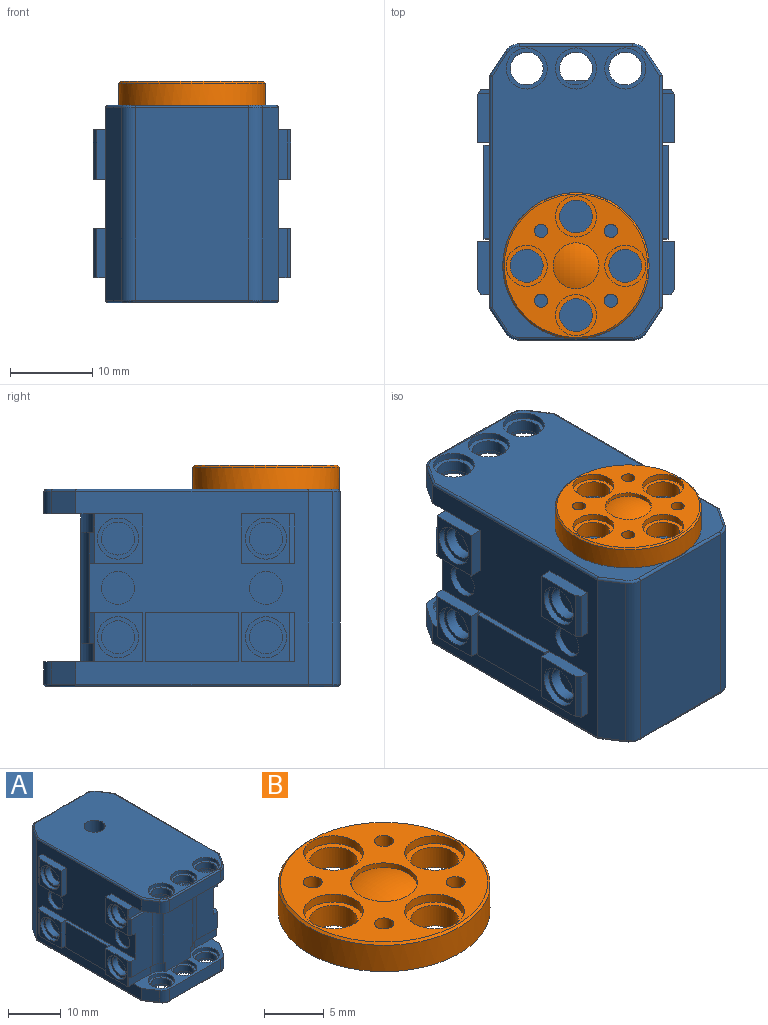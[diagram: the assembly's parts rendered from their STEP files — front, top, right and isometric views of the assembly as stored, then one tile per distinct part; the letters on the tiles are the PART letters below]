
ASSEMBLY  parts=2 mates=1
PART A: 203 faces, bbox 24x36x24 mm
  f0: cylinder r=8.9mm len=3.75mm, axis (0,0,1), area 0mm2, adj f1,f138
  f1: plane 35.6x20.4mm, normal (0,0,1), area 633.5mm2, adj f0,f38,f39,f40,f42,f43,f44,f61
  f2: plane 4x4mm, normal (1,0,0), area 12.6mm2, adj f10
  f3: plane 4x4mm, normal (1,0,0), area 12.6mm2, adj f11
  f4: plane 4x4mm, normal (1,0,0), area 12.6mm2, adj f12
  f5: plane 4x4mm, normal (1,0,0), area 12.6mm2, adj f13
  f6: plane 4x4mm, normal (-1,0,0), area 12.6mm2, adj f14
  f7: plane 4x4mm, normal (-1,0,0), area 12.6mm2, adj f15
  f8: plane 4x4mm, normal (-1,0,0), area 12.6mm2, adj f16
  f9: plane 4x4mm, normal (-1,0,0), area 12.6mm2, adj f17
  f10: cylinder r=2mm len=4mm, axis (1,0,0), area 17.6mm2, adj f2,f18
  f11: cylinder r=2mm len=4mm, axis (1,0,0), area 17.6mm2, adj f3,f19
  f12: cylinder r=2mm len=4mm, axis (1,0,0), area 17.6mm2, adj f4,f20
  f13: cylinder r=2mm len=4mm, axis (1,0,0), area 17.6mm2, adj f5,f21
  f14: cylinder r=2mm len=4mm, axis (1,0,0), area 17.6mm2, adj f6,f28
  f15: cylinder r=2mm len=4mm, axis (1,0,0), area 17.6mm2, adj f7,f29
  f16: cylinder r=2mm len=4mm, axis (1,0,0), area 17.6mm2, adj f8,f31
  f17: cylinder r=2mm len=4mm, axis (1,0,0), area 17.6mm2, adj f9,f32
  f18: plane 5x5mm, normal (1,0,0), area 7.1mm2, adj f10,f34
  f19: plane 5x5mm, normal (1,0,0), area 7.1mm2, adj f11,f35
  f20: plane 5x5mm, normal (1,0,0), area 7.1mm2, adj f12,f36
  f21: plane 5x5mm, normal (1,0,0), area 7.1mm2, adj f13,f37
  f22: plane 5x5mm, normal (0,0,1), area 7.1mm2, adj f26,f38
  f23: plane 5x5mm, normal (0,0,1), area 7.1mm2, adj f25,f39
  f24: plane 5x5mm, normal (0,0,1), area 7.1mm2, adj f27,f40
  f25: cylinder r=2mm len=4mm, axis (0,0,1), area 17.6mm2, adj f23,f41
  f26: cylinder r=2mm len=4mm, axis (0,0,1), area 17.6mm2, adj f22,f45
  f27: cylinder r=2mm len=4mm, axis (0,0,1), area 17.6mm2, adj f24,f46
  f28: plane 5x5mm, normal (-1,0,0), area 7.1mm2, adj f14,f47
  f29: plane 5x5mm, normal (-1,0,0), area 7.1mm2, adj f15,f48
  f30: plane 4x1mm, normal (0,0,1), area 2.8mm2, adj f49,f74
  f31: plane 5x5mm, normal (-1,0,0), area 7.1mm2, adj f16,f50
  f32: plane 5x5mm, normal (-1,0,0), area 7.1mm2, adj f17,f51
  f33: plane 4x1mm, normal (0,0,-1), area 2.8mm2, adj f49,f91
  f34: cylinder r=2.5mm len=5mm, axis (1,0,0), area 12.6mm2, adj f18,f54
  f35: cylinder r=2.5mm len=5mm, axis (1,0,0), area 12.6mm2, adj f19,f60
  f36: cylinder r=2.5mm len=5mm, axis (1,0,0), area 12.6mm2, adj f20,f63
  f37: cylinder r=2.5mm len=5mm, axis (1,0,0), area 12.6mm2, adj f21,f65
  f38: cylinder r=2.5mm len=5mm, axis (0,0,1), area 12.6mm2, adj f1,f22
  f39: cylinder r=2.5mm len=5mm, axis (0,0,1), area 12.6mm2, adj f1,f23
  f40: cylinder r=2.5mm len=5mm, axis (0,0,1), area 12.6mm2, adj f1,f24
  f41: plane 5x5mm, normal (0,0,-1), area 7.1mm2, adj f25,f74
  f42: revolved ~1.68x1.07mm, area 0.9mm2, adj f1,f43,f73,f77
  f43: cylinder r=0.3mm len=13.83mm, axis (1,0,0), area 6.5mm2, adj f1,f42,f44,f78
  f44: revolved ~1.68x1.07mm, area 0.9mm2, adj f1,f43,f61,f79
  f45: plane 5x5mm, normal (0,0,-1), area 7.1mm2, adj f26,f82
  f46: plane 5x5mm, normal (0,0,-1), area 7.1mm2, adj f27,f83
  f47: cylinder r=2.5mm len=5mm, axis (1,0,0), area 12.6mm2, adj f28,f84
  f48: cylinder r=2.5mm len=5mm, axis (1,0,0), area 12.6mm2, adj f29,f90
  f49: plane 18x8mm, normal (0,-1,0), area 138.4mm2, adj f30,f33,f56,f57,f58,f75,f81,f86
  f50: cylinder r=2.5mm len=5mm, axis (1,0,0), area 12.6mm2, adj f31,f99
  f51: cylinder r=2.5mm len=5mm, axis (1,0,0), area 12.6mm2, adj f32,f101
  f52: revolved ~1.68x1.07mm, area 0.9mm2, adj f111,f186,f187,f200
  f53: revolved ~1.68x1.07mm, area 0.9mm2, adj f112,f187,f188,f200
  f54: plane 6x5.84mm, normal (1,0,0), area 15.4mm2, adj f34,f59,f114,f115,f116
  f55: plane 6x0.66mm, normal (0.84,-0.54,0), area 3.3mm2, adj f56,f60,f80,f117,f118,f120
  f56: plane 8.54x1.53mm, normal (0,0,1), area 4.5mm2, adj f49,f55,f57,f80,f81,f117
  f57: cylinder r=2.5mm len=13.5mm, axis (0,0,1), area 31.3mm2, adj f49,f56,f58,f117
  f58: plane 8.54x1.53mm, normal (0,0,-1), area 4.5mm2, adj f49,f57,f59,f94,f95,f117
  f59: plane 6x0.66mm, normal (0.84,-0.54,0), area 3.3mm2, adj f54,f58,f94,f114,f116,f117
  f60: plane 6x5.84mm, normal (1,0,0), area 15.4mm2, adj f35,f55,f118,f119,f120
  f61: cylinder r=0.3mm len=3.1mm, axis (0.54,0.84,0), area 1.6mm2, adj f1,f44,f113,f121
  f62: plane 6x0.66mm, normal (0.84,0.54,0), area 4.7mm2, adj f63,f122,f123,f124
  f63: plane 6x5.84mm, normal (1,0,0), area 15.4mm2, adj f36,f62,f122,f124,f125
  f64: plane 6x0.66mm, normal (0.84,0.54,0), area 4.7mm2, adj f65,f126,f127,f128
  f65: plane 6x5.84mm, normal (1,0,0), area 15.4mm2, adj f37,f64,f126,f128,f129
  f66: plane 4x4mm, normal (1,0,0), area 12.6mm2, adj f130
  f67: plane 4x4mm, normal (1,0,0), area 12.6mm2, adj f131
  f68: plane 11.4x6mm, normal (1,0,0), area 68.4mm2, adj f132,f133,f134,f135
  f69: revolved ~1.68x1.07mm, area 0.9mm2, adj f137,f190,f191,f200
  f70: revolved ~1.68x1.07mm, area 0.9mm2, adj f1,f136,f137,f138
  f71: revolved ~1.68x1.07mm, area 0.9mm2, adj f139,f191,f192,f200
  f72: revolved ~1.68x1.07mm, area 0.9mm2, adj f1,f138,f139,f140
  f73: cylinder r=0.3mm len=3.1mm, axis (0.54,-0.84,0), area 1.6mm2, adj f1,f42,f141,f142
  f74: cylinder r=2.5mm len=5mm, axis (0,0,1), area 12.6mm2, adj f30,f41,f143
  f75: cylinder r=3.02mm len=2.63mm, axis (0,0,1), area 7.2mm2, adj f49,f76,f88,f143
  f76: plane 5.91x2.25mm, normal (0,-1,0), area 13.3mm2, adj f75,f88,f89,f143,f144
  f77: cylinder r=2mm len=2.7mm, axis (0,0,1), area 5.4mm2, adj f42,f78,f142,f143
  f78: plane 13.83x2.7mm, normal (0,-1,0), area 37.3mm2, adj f43,f77,f79,f143
  f79: cylinder r=2mm len=2.7mm, axis (0,0,1), area 5.4mm2, adj f44,f78,f121,f143
  f80: plane 5.91x2.25mm, normal (0,-1,0), area 13.3mm2, adj f55,f56,f81,f120,f143
  f81: cylinder r=3.02mm len=2.63mm, axis (0,0,1), area 7.2mm2, adj f49,f56,f80,f143
  f82: cylinder r=2.5mm len=5mm, axis (0,0,1), area 12.6mm2, adj f45,f143
  f83: cylinder r=2.5mm len=5mm, axis (0,0,1), area 12.6mm2, adj f46,f143
  f84: plane 6x5.84mm, normal (-1,0,0), area 15.4mm2, adj f47,f89,f144,f145,f146
  f85: plane 6x0.66mm, normal (-0.84,-0.54,0), area 3.3mm2, adj f86,f90,f93,f147,f148,f150
  f86: plane 8.54x1.53mm, normal (0,0,-1), area 4.5mm2, adj f49,f85,f87,f92,f93,f147
  f87: cylinder r=2.5mm len=13.5mm, axis (0,0,1), area 31.3mm2, adj f49,f86,f88,f147
  f88: plane 8.54x1.53mm, normal (0,0,1), area 4.5mm2, adj f49,f75,f76,f87,f89,f147
  f89: plane 6x0.66mm, normal (-0.84,-0.54,0), area 3.3mm2, adj f76,f84,f88,f144,f146,f147
  f90: plane 6x5.84mm, normal (-1,0,0), area 15.4mm2, adj f48,f85,f148,f149,f150
  f91: cylinder r=2.5mm len=5mm, axis (0,0,1), area 12.6mm2, adj f33,f109,f151
  f92: cylinder r=3.02mm len=2.63mm, axis (0,0,1), area 7.2mm2, adj f49,f86,f93,f151
  f93: plane 5.91x2.25mm, normal (0,-1,0), area 13.3mm2, adj f85,f86,f92,f150,f151
  f94: plane 5.91x2.25mm, normal (0,-1,0), area 13.3mm2, adj f58,f59,f95,f114,f151
  f95: cylinder r=3.02mm len=2.63mm, axis (0,0,1), area 7.2mm2, adj f49,f58,f94,f151
  f96: cylinder r=2.5mm len=5mm, axis (0,0,1), area 12.6mm2, adj f108,f151
  f97: cylinder r=2.5mm len=5mm, axis (0,0,1), area 12.6mm2, adj f110,f151
  f98: plane 6x0.66mm, normal (-0.84,0.54,0), area 4.7mm2, adj f99,f152,f153,f154
  f99: plane 6x5.84mm, normal (-1,0,0), area 15.4mm2, adj f50,f98,f152,f154,f155
  f100: plane 6x0.66mm, normal (-0.84,0.54,0), area 4.7mm2, adj f101,f156,f157,f158
  f101: plane 6x5.84mm, normal (-1,0,0), area 15.4mm2, adj f51,f100,f156,f158,f159
  f102: plane 4x4mm, normal (-1,0,0), area 12.6mm2, adj f160
  f103: plane 4x4mm, normal (-1,0,0), area 12.6mm2, adj f161
  f104: plane 11.4x6mm, normal (-1,0,0), area 68.4mm2, adj f162,f163,f164,f165
  f105: plane 4x4mm, normal (0,0,-1), area 12.6mm2, adj f166
  f106: plane 4x4mm, normal (0,0,-1), area 12.6mm2, adj f167
  f107: plane 4x4mm, normal (0,0,-1), area 12.6mm2, adj f168
  f108: plane 5x5mm, normal (0,0,1), area 7.1mm2, adj f96,f169
  f109: plane 5x5mm, normal (0,0,1), area 7.1mm2, adj f91,f170
  f110: plane 5x5mm, normal (0,0,1), area 7.1mm2, adj f97,f171
  f111: cylinder r=2mm len=2.7mm, axis (0,0,1), area 5.4mm2, adj f52,f151,f172,f173
  f112: cylinder r=2mm len=2.7mm, axis (0,0,1), area 5.4mm2, adj f53,f151,f173,f174
  f113: cylinder r=0.3mm len=28.3mm, axis (0,1,0), area 13.3mm2, adj f1,f61,f136,f175
  f114: plane 5.98x1.5mm, normal (0,0,-1), area 9mm2, adj f54,f59,f94,f115,f175
  f115: plane 6x1.5mm, normal (0,1,0), area 9mm2, adj f54,f114,f116,f175
  f116: plane 6.5x1.5mm, normal (0,0,1), area 9.6mm2, adj f54,f59,f115,f117,f175
  f117: plane 13.5x5.57mm, normal (0,-1,0), area 68.8mm2, adj f55,f56,f57,f58,f59,f116,f118,f175
  f118: plane 6.5x1.5mm, normal (0,0,-1), area 9.6mm2, adj f55,f60,f117,f119,f175
  f119: plane 6x1.5mm, normal (0,1,0), area 9mm2, adj f60,f118,f120,f175
  f120: plane 5.98x1.5mm, normal (0,0,1), area 9mm2, adj f55,f60,f80,f119,f175
  f121: plane 2.94x2.7mm, normal (0.84,-0.54,0), area 9.5mm2, adj f61,f79,f143,f175
  f122: plane 6.5x1.5mm, normal (0,0,-1), area 9.6mm2, adj f62,f63,f123,f125,f175
  f123: plane 6x1.07mm, normal (0,1,0), area 6.4mm2, adj f62,f122,f124,f175
  f124: plane 6.5x1.5mm, normal (0,0,1), area 9.6mm2, adj f62,f63,f123,f125,f175
  f125: plane 6x1.5mm, normal (0,-1,0), area 9mm2, adj f63,f122,f124,f175
  f126: plane 6.5x1.5mm, normal (0,0,-1), area 9.6mm2, adj f64,f65,f127,f129,f175
  f127: plane 6x1.07mm, normal (0,1,0), area 6.4mm2, adj f64,f126,f128,f175
  f128: plane 6.5x1.5mm, normal (0,0,1), area 9.6mm2, adj f64,f65,f127,f129,f175
  f129: plane 6x1.5mm, normal (0,-1,0), area 9mm2, adj f65,f126,f128,f175
  f130: cylinder r=2mm len=4mm, axis (1,0,0), area 10.1mm2, adj f66,f175
  f131: cylinder r=2mm len=4mm, axis (1,0,0), area 10.1mm2, adj f67,f175
  f132: plane 11.4x0.7mm, normal (0,0,1), area 8mm2, adj f68,f133,f135,f175
  f133: plane 6x0.7mm, normal (0,-1,0), area 4.2mm2, adj f68,f132,f134,f175
  f134: plane 11.4x0.7mm, normal (0,0,-1), area 8mm2, adj f68,f133,f135,f175
  f135: plane 6x0.7mm, normal (0,1,0), area 4.2mm2, adj f68,f132,f134,f175
  f136: cylinder r=0.3mm len=3.1mm, axis (-0.54,0.84,0), area 1.6mm2, adj f1,f70,f113,f176
  f137: cylinder r=2mm len=23.4mm, axis (0,0,-1), area 46.6mm2, adj f69,f70,f176,f177
  f138: cylinder r=0.3mm len=13.83mm, axis (-1,0,0), area 6mm2, adj f0,f1,f70,f72,f177
  f139: cylinder r=2mm len=23.4mm, axis (0,0,-1), area 46.6mm2, adj f71,f72,f177,f178
  f140: cylinder r=0.3mm len=3.1mm, axis (-0.54,-0.84,0), area 1.6mm2, adj f1,f72,f141,f178
  f141: cylinder r=0.3mm len=28.3mm, axis (0,-1,0), area 13.3mm2, adj f1,f73,f140,f179
  f142: plane 2.94x2.7mm, normal (-0.84,-0.54,0), area 9.5mm2, adj f73,f77,f143,f179
  f143: plane 21x6.03mm, normal (0,0,-1), area 47.8mm2, adj f49,f74,f75,f76,f77,f78,f79,f80
  f144: plane 5.98x1.5mm, normal (0,0,1), area 9mm2, adj f76,f84,f89,f145,f179
  f145: plane 6x1.5mm, normal (0,1,0), area 9mm2, adj f84,f144,f146,f179
  f146: plane 6.5x1.5mm, normal (0,0,-1), area 9.6mm2, adj f84,f89,f145,f147,f179
  f147: plane 13.5x5.57mm, normal (0,-1,0), area 68.8mm2, adj f85,f86,f87,f88,f89,f146,f148,f179
  f148: plane 6.5x1.5mm, normal (0,0,1), area 9.6mm2, adj f85,f90,f147,f149,f179
  f149: plane 6x1.5mm, normal (0,1,0), area 9mm2, adj f90,f148,f150,f179
  f150: plane 5.98x1.5mm, normal (0,0,-1), area 9mm2, adj f85,f90,f93,f149,f179
  f151: plane 21x6.03mm, normal (0,0,1), area 47.8mm2, adj f49,f91,f92,f93,f94,f95,f96,f97
  f152: plane 6.5x1.5mm, normal (0,0,1), area 9.6mm2, adj f98,f99,f153,f155,f179
  f153: plane 6x1.07mm, normal (0,1,0), area 6.4mm2, adj f98,f152,f154,f179
  f154: plane 6.5x1.5mm, normal (0,0,-1), area 9.6mm2, adj f98,f99,f153,f155,f179
  f155: plane 6x1.5mm, normal (0,-1,0), area 9mm2, adj f99,f152,f154,f179
  f156: plane 6.5x1.5mm, normal (0,0,1), area 9.6mm2, adj f100,f101,f157,f159,f179
  f157: plane 6x1.07mm, normal (0,1,0), area 6.4mm2, adj f100,f156,f158,f179
  f158: plane 6.5x1.5mm, normal (0,0,-1), area 9.6mm2, adj f100,f101,f157,f159,f179
  f159: plane 6x1.5mm, normal (0,-1,0), area 9mm2, adj f101,f156,f158,f179
  f160: cylinder r=2mm len=4mm, axis (1,0,0), area 10.1mm2, adj f102,f179
  f161: cylinder r=2mm len=4mm, axis (1,0,0), area 10.1mm2, adj f103,f179
  f162: plane 11.4x0.7mm, normal (0,0,1), area 8mm2, adj f104,f163,f165,f179
  f163: plane 6x0.7mm, normal (0,1,0), area 4.2mm2, adj f104,f162,f164,f179
  f164: plane 11.4x0.7mm, normal (0,0,-1), area 8mm2, adj f104,f163,f165,f179
  f165: plane 6x0.7mm, normal (0,-1,0), area 4.2mm2, adj f104,f162,f164,f179
  f166: cylinder r=2mm len=4mm, axis (0,0,-1), area 27.6mm2, adj f105,f180
  f167: cylinder r=2mm len=4mm, axis (0,0,-1), area 27.6mm2, adj f106,f181
  f168: cylinder r=2mm len=4mm, axis (0,0,-1), area 27.6mm2, adj f107,f182
  f169: cylinder r=2mm len=4mm, axis (0,0,1), area 17.6mm2, adj f108,f183
  f170: cylinder r=2mm len=4mm, axis (0,0,1), area 17.6mm2, adj f109,f184
  f171: cylinder r=2mm len=4mm, axis (0,0,1), area 17.6mm2, adj f110,f185
  f172: plane 2.94x2.7mm, normal (-0.84,-0.54,0), area 9.5mm2, adj f111,f151,f179,f186
  f173: plane 13.83x2.7mm, normal (0,-1,0), area 37.3mm2, adj f111,f112,f151,f187
  f174: plane 2.94x2.7mm, normal (0.84,-0.54,0), area 9.5mm2, adj f112,f151,f175,f188
  f175: plane 28.3x23.4mm, normal (1,0,0), area 383mm2, adj f113,f114,f115,f116,f117,f118,f119,f120
  f176: plane 23.4x2.94mm, normal (0.84,0.54,0), area 82mm2, adj f136,f137,f175,f190
  f177: plane 23.4x13.83mm, normal (0,1,0), area 323.6mm2, adj f137,f138,f139,f191
  f178: plane 23.4x2.94mm, normal (-0.84,0.54,0), area 82mm2, adj f139,f140,f179,f192
  f179: plane 28.3x23.4mm, normal (-1,0,0), area 383mm2, adj f141,f142,f143,f144,f145,f146,f147,f148
  f180: plane 5x5mm, normal (0,0,-1), area 7.1mm2, adj f166,f194
  f181: plane 5x5mm, normal (0,0,-1), area 7.1mm2, adj f167,f195
  f182: plane 5x5mm, normal (0,0,-1), area 7.1mm2, adj f168,f196
  f183: plane 5x5mm, normal (0,0,-1), area 7.1mm2, adj f169,f197
  f184: plane 5x5mm, normal (0,0,-1), area 7.1mm2, adj f170,f198
  f185: plane 5x5mm, normal (0,0,-1), area 7.1mm2, adj f171,f199
  f186: cylinder r=0.3mm len=3.1mm, axis (-0.54,0.84,0), area 1.6mm2, adj f52,f172,f193,f200
  f187: cylinder r=0.3mm len=13.83mm, axis (-1,0,0), area 6.5mm2, adj f52,f53,f173,f200
  f188: cylinder r=0.3mm len=3.1mm, axis (-0.54,-0.84,0), area 1.6mm2, adj f53,f174,f189,f200
  f189: cylinder r=0.3mm len=28.3mm, axis (0,-1,0), area 13.3mm2, adj f175,f188,f190,f200
  f190: cylinder r=0.3mm len=3.1mm, axis (0.54,-0.84,0), area 1.6mm2, adj f69,f176,f189,f200
  f191: cylinder r=0.3mm len=13.83mm, axis (1,0,0), area 6.5mm2, adj f69,f71,f177,f200
  f192: cylinder r=0.3mm len=3.1mm, axis (0.54,0.84,0), area 1.6mm2, adj f71,f178,f193,f200
  f193: cylinder r=0.3mm len=28.3mm, axis (0,1,0), area 13.3mm2, adj f179,f186,f192,f200
  f194: cylinder r=2.5mm len=5mm, axis (0,0,-1), area 12.6mm2, adj f180,f200
  f195: cylinder r=2.5mm len=5mm, axis (0,0,-1), area 12.6mm2, adj f181,f200
  f196: cylinder r=2.5mm len=5mm, axis (0,0,-1), area 12.6mm2, adj f182,f200
  f197: cylinder r=2.5mm len=5mm, axis (0,0,-1), area 12.6mm2, adj f183,f200
  f198: cylinder r=2.5mm len=5mm, axis (0,0,-1), area 12.6mm2, adj f184,f200
  f199: cylinder r=2.5mm len=5mm, axis (0,0,-1), area 12.6mm2, adj f185,f200
  f200: plane 35.4x20.4mm, normal (0,0,-1), area 586.6mm2, adj f52,f53,f69,f71,f186,f187,f188,f189
  f201: cylinder r=2mm len=5mm, axis (0,0,1), area 62.8mm2, adj f1,f202
  f202: plane 4x4mm, normal (0,0,1), area 12.6mm2, adj f201
PART B: 22 faces, bbox 17.8x17.8x2.9 mm
  f0: revolved ~5.62x5.6mm, area 25.4mm2, adj f13
  f1: plane 5x5mm, normal (0,0,1), area 7.1mm2, adj f2,f3
  f2: cylinder r=2mm len=4mm, axis (0,0,1), area 26.4mm2, adj f1,f21
  f3: cylinder r=2.5mm len=5mm, axis (0,0,1), area 12.6mm2, adj f1,f19
  f4: plane 5x5mm, normal (0,0,1), area 7.1mm2, adj f5,f6
  f5: cylinder r=2mm len=4mm, axis (0,0,1), area 26.4mm2, adj f4,f21
  f6: cylinder r=2.5mm len=5mm, axis (0,0,1), area 12.6mm2, adj f4,f19
  f7: plane 5x5mm, normal (0,0,1), area 7.1mm2, adj f8,f9
  f8: cylinder r=2mm len=4mm, axis (0,0,1), area 26.4mm2, adj f7,f21
  f9: cylinder r=2.5mm len=5mm, axis (0,0,1), area 12.6mm2, adj f7,f19
  f10: plane 5x5mm, normal (0,0,1), area 7.1mm2, adj f11,f12
  f11: cylinder r=2mm len=4mm, axis (0,0,1), area 26.4mm2, adj f10,f21
  f12: cylinder r=2.5mm len=5mm, axis (0,0,1), area 12.6mm2, adj f10,f19
  f13: cylinder r=2.8mm len=5.6mm, axis (0,0,1), area 8.8mm2, adj f0,f19
  f14: cone r=8.9mm half-angle=45deg, axis (0,0,-1), area 15.6mm2, adj f15,f19
  f15: cylinder r=8.9mm len=17.8mm, axis (0,0,1), area 151mm2, adj f14,f21
  f16: cylinder r=0.8mm len=2.9mm, axis (0,0,1), area 14.6mm2, adj f19,f21
  f17: cylinder r=0.8mm len=2.9mm, axis (0,0,1), area 14.6mm2, adj f19,f21
  f18: cylinder r=0.8mm len=2.9mm, axis (0,0,1), area 14.6mm2, adj f19,f21
  f19: plane 17.4x17.4mm, normal (0,0,1), area 126.6mm2, adj f3,f6,f9,f12,f13,f14,f16,f17
  f20: cylinder r=0.8mm len=2.9mm, axis (0,0,1), area 14.6mm2, adj f19,f21
  f21: plane 17.8x17.8mm, normal (0,0,-1), area 190.5mm2, adj f2,f5,f8,f11,f15,f16,f17,f18
PLACE A rot(axis=(0,0,1),180deg) t=(-14.69,-4.03,18.78)mm
PLACE B t=(-14.69,-4.03,18.68)mm
MATE revolute B.f13 <-> A.f0  axis (0,0,-1) through (-14.69,-4.03,30.78)mm
